# Revit family: Electronics_Expanders_Biamp_Tesira_AVB-USB-with-Bluetooth-Wireless-Technology_EX-UBT___
name_source: partatom
category: Communication Devices
units: mm (PartAtom-declared; Revit-internal decimal feet)

## family parameters
Cut with Voids When Loaded = No
Host = Face
Maintain Annotation Orientation = No
OmniClass Number = 23.85.10.11
OmniClass Title = Audio Information, Sound Signals
Part Type = Normal
Room Calculation Point = No
Round Connector Dimension = Use Diameter
Shared = No

## types (1)
- EX-UBT
    Altitude = 0-10,000 ft (0-3000m) MSL
    Apparent Load = 0 VA
    BER/EDR = 6.43 dBm (EIRP)
    BLE = 7.69 dBm (EIRP)
    Bluetooth Mode = Bluetooth Classic
    Bluetooth Supported Codecs = mSBC (16 kHz), SBC (48 kHz), AAC (48 kHz), aptX (48 kHz)
    Bluetooth Supported Profiles = Hands-Free Profile 1.7 (HFP) / Advanced Audio /  Distribution Profile 1.3 (A2DP)
    Bluetooth Version = 4.2, Class 2
    Compliance = FCC Part 15B (USA) CE marked (Europe) UL and C-UL listed (USA and Canada) RoHS Directive (Europe)
    Connector Description = PoE (IEEE 802.3at Class 2, 7W)
    Default Elevation = 4' - 0"
    Depth = 0' - 4 3/16"
    Description = Tesira® EX-UBT AVB/USB Expander with Bluetooth® Wireless Technology
    Frequency Band = 2,402 to 2,480 MHz
    Height = 0' - 1 1/16"
    Housing Material = Biamp - Plastic - Black
    Humidity = 0-95% relative humidity (non-condensing)
    Indicators = Power Indicator (Green/Red LED) Wireless Indicator (Blue/Red LED)
    Manufacturer = Biamp
    Max Power Consumption = 0 W
    Model = Tesira EX-UBT
    Network Connection = RJ-45 with Ethernet cable (Cat 5e and above)
    Number of Poles = 1
    Power Factor = 1
    Product Documentation Link = https://downloads.biamp.com
    Product Page URL = https://www.biamp.com
    Product data url = https://www.bimobject.com
    Receive Sensitivity = -88 dBm 0.1% BER
    Temperature Range = 32 - 104° F (0 - 40° C)
    URL = https://www.biamp.com
    USB Bit Depth = 16-bit / 24-bit
    USB Number of Channels = up to 8
    USB Sample Rate = 48kHz
    Voltage = 0 V
    Weight = 0.20 lbf
    Width = 0' - 2 1/2"
    Wireless Range = Up to 100 feet (30 m)

## geometry (parser evidence)
native form markers: Sweep x2
no freeform markers — native parametric forms only
